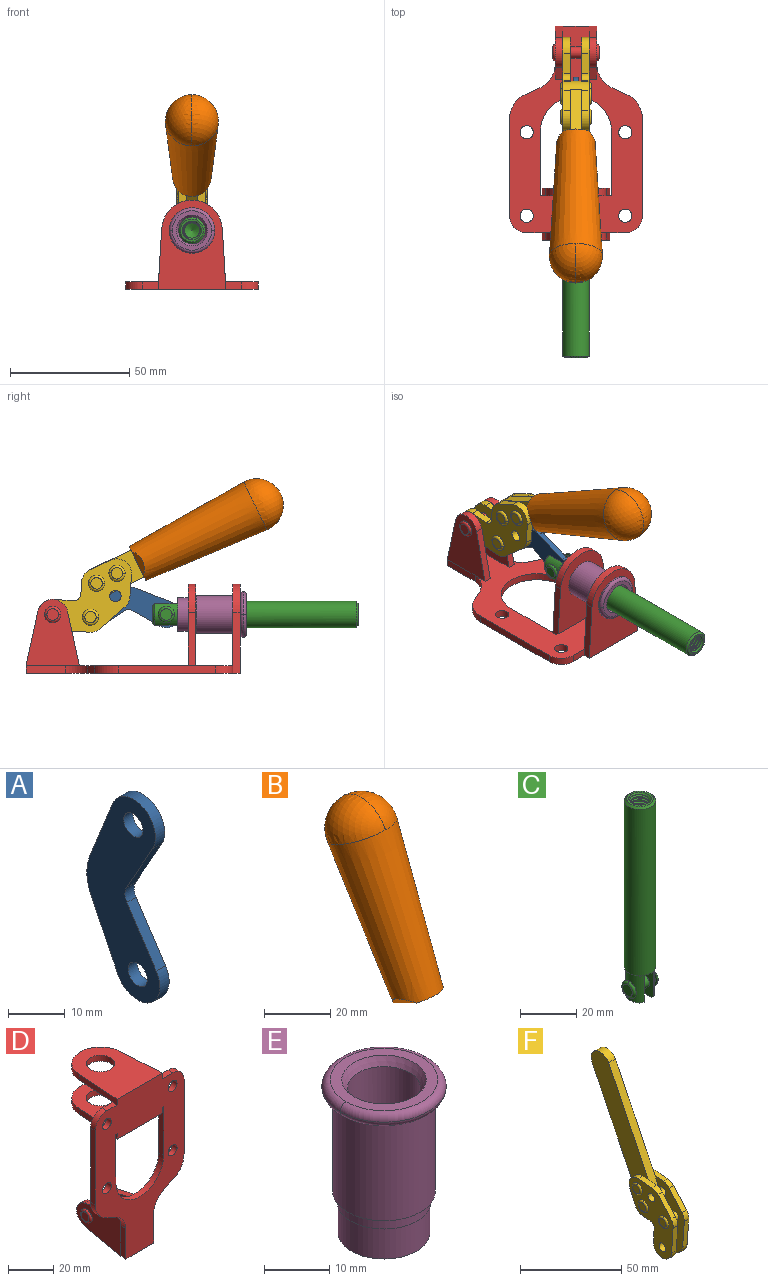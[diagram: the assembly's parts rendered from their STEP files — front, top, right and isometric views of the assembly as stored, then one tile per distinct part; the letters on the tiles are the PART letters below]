
ASSEMBLY  parts=6 mates=6
PART A: 12 faces, bbox 2.3x18.2x42.8 mm
  f0: cylinder r=2.4mm len=4.8mm, axis (1,0,0), area 34.9mm2, adj f4,f11
  f1: cylinder r=10.41mm len=8.47mm, axis (1,0,0), area 20.2mm2, adj f4,f9,f10,f11
  f2: cylinder r=3.05mm len=3.16mm, axis (1,0,0), area 7.7mm2, adj f4,f6,f7,f11
  f3: cylinder r=2.4mm len=4.8mm, axis (1,0,0), area 34.9mm2, adj f4,f11
  f4: plane 42.81x18.23mm, normal (-1,0,0), area 414.1mm2, adj f0,f1,f2,f3,f5,f6,f7,f8
  f5: cylinder r=5.54mm len=10.67mm, axis (1,0,0), area 41.8mm2, adj f4,f6,f10,f11
  f6: plane 11.66x6.53mm, normal (0,-0.87,-0.49), area 30.9mm2, adj f2,f4,f5,f11
  f7: plane 11.17x7.33mm, normal (0,-0.84,0.55), area 30.9mm2, adj f2,f4,f8,f11
  f8: cylinder r=5.54mm len=10.51mm, axis (1,0,0), area 41.8mm2, adj f4,f7,f9,f11
  f9: plane 13.67x6.67mm, normal (0,0.9,-0.44), area 35.1mm2, adj f1,f4,f8,f11
  f10: plane 14.1x5.7mm, normal (0,0.93,0.37), area 35.1mm2, adj f1,f4,f5,f11
  f11: plane 42.81x18.23mm, normal (1,0,0), area 414.1mm2, adj f0,f1,f2,f3,f5,f6,f7,f8
PART B: 11 faces, bbox 22.3x42.6x64.5 mm
  f0: sphere r=11.13mm, area 411.4mm2, adj f1,f8
  f1: cone r=11.11mm half-angle=3.3deg, axis (0,0.44,0.9), area 3251.8mm2, adj f0,f7,f8,f9,f10
  f2: cylinder r=6.16mm len=11.7mm, axis (1,0,0), area 89.5mm2, adj f3,f4,f5,f6
  f3: plane 60.23x36.75mm, normal (-1,0,0), area 763.6mm2, adj f2,f4,f6,f10
  f4: plane 51.37x25.05mm, normal (0,0.9,-0.44), area 264.2mm2, adj f2,f3,f5,f10
  f5: plane 60.23x36.75mm, normal (1,0,0), area 763.6mm2, adj f2,f4,f6,f10
  f6: plane 51.37x25.05mm, normal (0,-0.9,0.44), area 264.2mm2, adj f2,f3,f5,f10
  f7: plane 9.95x5.95mm, normal (0.71,-0.31,-0.64), area 25.8mm2, adj f1,f10
  f8: sphere r=11.13mm, area 411.4mm2, adj f0,f1
  f9: plane 9.95x5.95mm, normal (-0.71,-0.31,-0.64), area 25.8mm2, adj f1,f10
  f10: plane 14.27x11.38mm, normal (0,-0.44,-0.9), area 106.7mm2, adj f1,f3,f4,f5,f6,f7,f9
PART C: 48 faces, bbox 12.6x11.1x86.1 mm
  f0: torus R=2.41mm, axis (-1,0,0), area 15mm2, adj f30,f32,f34
  f1: torus R=2.41mm, axis (-1,0,0), area 15mm2, adj f29,f31,f33
  f2: cylinder r=5.54mm len=72.39mm, axis (0,0,1), area 2518.5mm2, adj f3,f4,f42,f43
  f3: cone r=5.54mm half-angle=45deg, axis (0,0,1), area 7.6mm2, adj f2,f5,f41
  f4: cone r=5.54mm half-angle=45deg, axis (0,0,-1), area 34.9mm2, adj f2,f39
  f5: cylinder r=5.08mm len=11.48mm, axis (0,0,1), area 108.3mm2, adj f3,f7,f8,f41
  f6: cylinder r=2.41mm len=4.83mm, axis (-1,0,0), area 71.2mm2, adj f40,f41
  f7: cylinder r=2.41mm len=4.83mm, axis (-1,0,0), area 7.6mm2, adj f5,f34
  f8: cone r=5.08mm half-angle=45deg, axis (0,0,1), area 10.6mm2, adj f5,f37,f41
  f9: cone r=3.98mm half-angle=45deg, axis (0,0,1), area 17.6mm2, adj f27,f39,f45,f46,f47
  f10: cylinder r=2.41mm len=4.83mm, axis (-1,0,0), area 7.6mm2, adj f33,f38
  f11: cylinder r=3.2mm len=6.4mm, axis (0,0,1), area 78.4mm2, adj f12,f28,f44,f45,f47
  f12: cylinder r=3.2mm len=6.4mm, axis (0,0,1), area 10.5mm2, adj f11,f13,f45,f47
  f13: cylinder r=3.2mm len=6.4mm, axis (0,0,1), area 10.5mm2, adj f12,f14,f45,f47
  f14: cylinder r=3.2mm len=6.4mm, axis (0,0,1), area 10.5mm2, adj f13,f15,f45,f47
  f15: cylinder r=3.2mm len=6.4mm, axis (0,0,1), area 10.5mm2, adj f14,f16,f45,f47
  f16: cylinder r=3.2mm len=6.4mm, axis (0,0,1), area 10.5mm2, adj f15,f17,f45,f47
  f17: cylinder r=3.2mm len=6.4mm, axis (0,0,1), area 10.5mm2, adj f16,f18,f45,f47
  f18: cylinder r=3.2mm len=6.4mm, axis (0,0,1), area 10.5mm2, adj f17,f19,f45,f47
  f19: cylinder r=3.2mm len=6.4mm, axis (0,0,1), area 10.5mm2, adj f18,f20,f45,f47
  f20: cylinder r=3.2mm len=6.4mm, axis (0,0,1), area 10.5mm2, adj f19,f21,f45,f47
  f21: cylinder r=3.2mm len=6.4mm, axis (0,0,1), area 10.5mm2, adj f20,f22,f45,f47
  f22: cylinder r=3.2mm len=6.4mm, axis (0,0,1), area 10.5mm2, adj f21,f23,f45,f47
  f23: cylinder r=3.2mm len=6.4mm, axis (0,0,1), area 10.5mm2, adj f22,f24,f45,f47
  f24: cylinder r=3.2mm len=6.4mm, axis (0,0,1), area 10.5mm2, adj f23,f25,f45,f47
  f25: cylinder r=3.2mm len=6.4mm, axis (0,0,1), area 10.5mm2, adj f24,f26,f45,f47
  f26: cylinder r=3.2mm len=6.4mm, axis (0,0,1), area 10.5mm2, adj f25,f27,f45,f47
  f27: cylinder r=3.2mm len=6.4mm, axis (0,0,1), area 7.4mm2, adj f9,f26,f45,f47
  f28: cone r=3.2mm half-angle=60deg, axis (0,0,1), area 37.2mm2, adj f11
  f29: plane 4.83x4.83mm, normal (-1,0,0), area 18.3mm2, adj f1,f31
  f30: plane 4.83x4.83mm, normal (1,0,0), area 18.3mm2, adj f0,f32
  f31: torus R=2.41mm, axis (-1,0,0), area 15mm2, adj f1,f29,f33
  f32: torus R=2.41mm, axis (-1,0,0), area 15mm2, adj f0,f30,f34
  f33: plane 6.83x6.83mm, normal (1,0,0), area 18.3mm2, adj f1,f10,f31
  f34: plane 6.83x6.83mm, normal (-1,0,0), area 18.3mm2, adj f0,f7,f32
  f35: cone r=5.08mm half-angle=45deg, axis (0,0,1), area 10.6mm2, adj f36,f38,f40
  f36: plane 7.25x1.97mm, normal (0,0,-1), area 10mm2, adj f35,f40
  f37: plane 7.25x1.97mm, normal (0,0,-1), area 10mm2, adj f8,f41
  f38: cylinder r=5.08mm len=11.48mm, axis (0,0,1), area 108.3mm2, adj f10,f35,f40,f42
  f39: plane 9.55x9.55mm, normal (0,0,1), area 22mm2, adj f4,f9
  f40: plane 12.76x10.09mm, normal (1,0,0), area 95.7mm2, adj f6,f35,f36,f38,f42,f43
  f41: plane 12.76x10.09mm, normal (-1,0,0), area 95.7mm2, adj f3,f5,f6,f8,f37,f43
  f42: cone r=5.54mm half-angle=45deg, axis (0,0,1), area 7.6mm2, adj f2,f38,f40
  f43: plane 11.07x4.7mm, normal (0,0,-1), area 50.4mm2, adj f2,f40,f41
  f44: plane 0.89x0.62mm, normal (-1,0,0), area 0.3mm2, adj f11,f45,f46,f47
  f45: bspline ~24.8x7.63mm, area 266.6mm2, adj f9,f11,f12,f13,f14,f15,f16,f17
  f46: bspline ~24.87x7.63mm, area 73.6mm2, adj f9,f44,f45,f47
  f47: bspline ~24.98x7.63mm, area 272.5mm2, adj f9,f11,f12,f13,f14,f15,f16,f17
PART D: 55 faces, bbox 55.7x37.4x89.8 mm
  f0: torus R=2.41mm, axis (-1,0,0), area 15mm2, adj f11,f15,f25
  f1: torus R=2.41mm, axis (-1,0,0), area 15mm2, adj f10,f12,f22
  f2: cylinder r=2.78mm len=5.56mm, axis (0,-1,0), area 54.2mm2, adj f30,f54
  f3: cylinder r=14.99mm len=29.97mm, axis (0,-1,0), area 145.9mm2, adj f30,f49,f53,f54
  f4: cylinder r=2.78mm len=5.56mm, axis (0,-1,0), area 54.2mm2, adj f30,f54
  f5: cylinder r=2.78mm len=5.56mm, axis (0,-1,0), area 54.2mm2, adj f30,f54
  f6: cylinder r=2.78mm len=5.56mm, axis (0,-1,0), area 54.2mm2, adj f30,f54
  f7: cylinder r=6.35mm len=12.7mm, axis (0,0,1), area 123.6mm2, adj f27,f51
  f8: cylinder r=6.35mm len=12.7mm, axis (0,0,-1), area 124.7mm2, adj f21,f35
  f9: cylinder r=2.41mm len=11.18mm, axis (-1,0,0), area 169.4mm2, adj f16,f19
  f10: plane 4.83x4.83mm, normal (1,0,0), area 18.3mm2, adj f1,f12
  f11: plane 4.83x4.83mm, normal (-1,0,0), area 18.3mm2, adj f0,f15
  f12: torus R=2.41mm, axis (-1,0,0), area 15mm2, adj f1,f10,f22
  f13: cylinder r=6.35mm len=12.41mm, axis (1,0,0), area 53.4mm2, adj f18,f19,f22,f23
  f14: cylinder r=6.35mm len=12.41mm, axis (-1,0,0), area 53.4mm2, adj f16,f17,f24,f25
  f15: torus R=2.41mm, axis (-1,0,0), area 15mm2, adj f0,f11,f25
  f16: plane 27.86x22.35mm, normal (1,0,0), area 425.4mm2, adj f9,f14,f17,f24,f30
  f17: plane 22.86x4.97mm, normal (0,0.21,0.98), area 72.5mm2, adj f14,f16,f25,f30
  f18: plane 22.86x4.97mm, normal (0,0.21,0.98), area 72.5mm2, adj f13,f19,f22,f30
  f19: plane 27.86x22.35mm, normal (-1,0,0), area 425.4mm2, adj f9,f13,f18,f23,f30
  f20: cylinder r=12.7mm len=25.35mm, axis (0,0,-1), area 119.8mm2, adj f21,f34,f35,f36
  f21: plane 34.21x28.07mm, normal (0,0,-1), area 702.4mm2, adj f8,f20,f30,f34,f36
  f22: plane 27.96x22.45mm, normal (1,0,0), area 407.2mm2, adj f1,f12,f13,f18,f23,f30,f42,f43
  f23: plane 22.86x4.97mm, normal (0,0.21,-0.98), area 72.5mm2, adj f13,f19,f22,f44
  f24: plane 22.86x4.97mm, normal (0,0.21,-0.98), area 72.5mm2, adj f14,f16,f25,f44
  f25: plane 27.86x22.35mm, normal (-1,0,0), area 407.1mm2, adj f0,f14,f15,f17,f24,f30,f45,f46
  f26: plane 3.1x0.95mm, normal (0,0,-1), area 2.7mm2, adj f30,f49,f50,f54
  f27: plane 34.21x28.07mm, normal (0,0,1), area 702.4mm2, adj f7,f28,f30,f50,f52
  f28: cylinder r=12.7mm len=25.35mm, axis (0,0,1), area 118.8mm2, adj f27,f50,f51,f52
  f29: plane 3.1x0.95mm, normal (0,0,-1), area 2.7mm2, adj f30,f52,f53,f54
  f30: plane 86.54x55.63mm, normal (0,1,0), area 2362.9mm2, adj f2,f3,f4,f5,f6,f16,f17,f18
  f31: plane 40.56x3.1mm, normal (-1,0,0), area 125.7mm2, adj f30,f32,f48,f54
  f32: cylinder r=7.11mm len=7.11mm, axis (0,-1,0), area 34.6mm2, adj f30,f31,f33,f54
  f33: plane 6.67x3.1mm, normal (0,0,1), area 20.4mm2, adj f30,f32,f34,f54
  f34: plane 25.39x3.13mm, normal (-1,0.06,0), area 79.5mm2, adj f20,f21,f33,f35,f54
  f35: plane 37.31x28.45mm, normal (0,0,1), area 789.9mm2, adj f8,f20,f34,f36,f54
  f36: plane 25.39x3.13mm, normal (1,0.06,0), area 79.5mm2, adj f20,f21,f35,f37,f54
  f37: plane 6.67x3.1mm, normal (0,0,1), area 20.4mm2, adj f30,f36,f38,f54
  f38: cylinder r=7.11mm len=7.11mm, axis (0,-1,0), area 34.6mm2, adj f30,f37,f39,f54
  f39: plane 40.56x3.1mm, normal (1,0,0), area 125.7mm2, adj f30,f38,f40,f54
  f40: cylinder r=11.18mm len=10.16mm, axis (0,-1,0), area 39.5mm2, adj f30,f39,f41,f54
  f41: plane 6.09x3.1mm, normal (0.42,0,-0.91), area 20.8mm2, adj f30,f40,f42,f54
  f42: cylinder r=11.18mm len=9.41mm, axis (0,-1,0), area 37.2mm2, adj f22,f30,f41,f43,f54
  f43: plane 16.5x3.1mm, normal (1,0,0), area 51.1mm2, adj f22,f42,f44,f54
  f44: plane 17.37x3.1mm, normal (0,0,-1), area 53.8mm2, adj f23,f24,f30,f43,f45,f54
  f45: plane 16.5x3.1mm, normal (-1,0,0), area 51.1mm2, adj f25,f44,f46,f54
  f46: cylinder r=11.18mm len=9.41mm, axis (0,-1,0), area 37.2mm2, adj f25,f30,f45,f47,f54
  f47: plane 6.09x3.1mm, normal (-0.42,0,-0.91), area 20.8mm2, adj f30,f46,f48,f54
  f48: cylinder r=11.18mm len=10.16mm, axis (0,-1,0), area 39.5mm2, adj f30,f31,f47,f54
  f49: plane 26.54x3.1mm, normal (-1,0,0), area 82.3mm2, adj f3,f26,f30,f54
  f50: plane 25.39x3.1mm, normal (1,0.06,0), area 78.8mm2, adj f26,f27,f28,f51,f54
  f51: plane 37.31x28.45mm, normal (0,0,-1), area 789.9mm2, adj f7,f28,f50,f52,f54
  f52: plane 25.39x3.1mm, normal (-1,0.06,0), area 78.8mm2, adj f27,f28,f29,f51,f54
  f53: plane 26.54x3.1mm, normal (1,0,0), area 82.3mm2, adj f3,f29,f30,f54
  f54: plane 89.66x55.63mm, normal (0,-1,0), area 2678.5mm2, adj f2,f3,f4,f5,f6,f26,f29,f31
PART E: 15 faces, bbox 20.6x20.6x28.7 mm
  f0: torus R=8.26mm, axis (0,0,1), area 56.8mm2, adj f1,f10,f12
  f1: torus R=8.26mm, axis (0,0,1), area 56.8mm2, adj f0,f6,f13
  f2: cylinder r=5.59mm len=25.91mm, axis (0,0,1), area 909.6mm2, adj f3,f4
  f3: cone r=6.86mm half-angle=45deg, axis (0,0,-1), area 70.2mm2, adj f2,f14
  f4: cone r=6.47mm half-angle=30deg, axis (0,0,1), area 66.7mm2, adj f2,f13
  f5: cylinder r=7.04mm len=14.07mm, axis (0,0,1), area 252.6mm2, adj f11,f14
  f6: torus R=8.26mm, axis (0,0,1), area 56.8mm2, adj f1,f12,f13
  f7: cylinder r=7.16mm len=14.33mm, axis (0,0,1), area 91.5mm2, adj f9,f11
  f8: cylinder r=7.86mm len=18.42mm, axis (0,0,1), area 909.6mm2, adj f9,f10
  f9: plane 15.72x15.72mm, normal (0,0,-1), area 33mm2, adj f7,f8
  f10: plane 16.51x16.51mm, normal (0,0,-1), area 19.9mm2, adj f0,f8,f12
  f11: plane 14.33x14.33mm, normal (0,0,-1), area 5.7mm2, adj f5,f7
  f12: torus R=8.26mm, axis (0,0,1), area 56.8mm2, adj f0,f6,f10
  f13: plane 16.51x16.51mm, normal (0,0,1), area 82.7mm2, adj f1,f4,f6
  f14: plane 14.07x14.07mm, normal (0,0,-1), area 7.8mm2, adj f3,f5
PART F: 59 faces, bbox 12.9x60.2x99.6 mm
  f0: torus R=2.39mm, axis (-1,0,0), area 14.9mm2, adj f20,f43,f51
  f1: torus R=2.39mm, axis (-1,0,0), area 14.9mm2, adj f19,f42,f51
  f2: torus R=2.39mm, axis (-1,0,0), area 14.9mm2, adj f18,f35,f51
  f3: torus R=2.39mm, axis (-1,0,0), area 14.9mm2, adj f14,f17,f23
  f4: torus R=2.39mm, axis (-1,0,0), area 14.9mm2, adj f13,f16,f23
  f5: torus R=2.39mm, axis (-1,0,0), area 14.9mm2, adj f12,f15,f23
  f6: cylinder r=2.39mm len=4.78mm, axis (1,0,0), area 46.5mm2, adj f48,f50,f51
  f7: cylinder r=2.39mm len=4.78mm, axis (1,0,0), area 46.5mm2, adj f50,f51
  f8: cylinder r=6.35mm len=12.68mm, axis (1,0,0), area 61.8mm2, adj f38,f39,f50,f51
  f9: cylinder r=2.39mm len=4.78mm, axis (-1,0,0), area 70.5mm2, adj f46,f50
  f10: cylinder r=2.39mm len=4.78mm, axis (-1,0,0), area 46.5mm2, adj f23,f45,f46
  f11: cylinder r=2.39mm len=4.78mm, axis (-1,0,0), area 46.5mm2, adj f23,f46
  f12: plane 4.78x4.78mm, normal (1,0,0), area 17.9mm2, adj f5,f15
  f13: plane 4.78x4.78mm, normal (1,0,0), area 17.9mm2, adj f4,f16
  f14: plane 4.78x4.78mm, normal (1,0,0), area 17.9mm2, adj f3,f17
  f15: torus R=2.39mm, axis (-1,0,0), area 14.9mm2, adj f5,f12,f23
  f16: torus R=2.39mm, axis (-1,0,0), area 14.9mm2, adj f4,f13,f23
  f17: torus R=2.39mm, axis (-1,0,0), area 14.9mm2, adj f3,f14,f23
  f18: plane 4.78x4.78mm, normal (-1,0,0), area 17.9mm2, adj f2,f35
  f19: plane 4.78x4.78mm, normal (-1,0,0), area 17.9mm2, adj f1,f42
  f20: plane 4.78x4.78mm, normal (-1,0,0), area 17.9mm2, adj f0,f43
  f21: plane 2.26x0.2mm, normal (1,0,0), area 0.2mm2, adj f31,f44
  f22: plane 2.26x0.2mm, normal (-1,0,0), area 0.2mm2, adj f41,f44
  f23: plane 39.37x30.77mm, normal (1,0,0), area 565.5mm2, adj f3,f4,f5,f10,f11,f15,f16,f17
  f24: cylinder r=6.1mm len=4.15mm, axis (-1,0,0), area 14.7mm2, adj f23,f25,f32,f46
  f25: plane 10.25x9.01mm, normal (0,-0.75,0.66), area 42.3mm2, adj f23,f24,f26,f46
  f26: cylinder r=6.35mm len=4.64mm, axis (-1,0,0), area 15.6mm2, adj f23,f25,f27,f46
  f27: plane 15.84x3.1mm, normal (0,-1,-0.07), area 49.2mm2, adj f23,f26,f28,f46
  f28: cylinder r=6.35mm len=12.68mm, axis (-1,0,0), area 61.8mm2, adj f23,f27,f29,f46
  f29: plane 8.11x3.1mm, normal (0,1,0.07), area 25.2mm2, adj f23,f28,f30,f46
  f30: cylinder r=3.05mm len=3.25mm, axis (-1,0,0), area 14.8mm2, adj f23,f29,f31,f46
  f31: plane 5.99x3.1mm, normal (0,0.07,-1), area 18.6mm2, adj f21,f23,f30,f44,f46
  f32: plane 9.5x3.1mm, normal (0,-0.07,1), area 29.5mm2, adj f23,f24,f33,f46,f47
  f33: cylinder r=6.1mm len=8.63mm, axis (-1,0,0), area 39.1mm2, adj f23,f32,f34,f47
  f34: plane 8.65x3.96mm, normal (0,0.91,-0.42), area 29.5mm2, adj f23,f33,f44,f47
  f35: torus R=2.39mm, axis (-1,0,0), area 14.9mm2, adj f2,f18,f51
  f36: plane 10.25x9.01mm, normal (0,-0.75,0.66), area 42.3mm2, adj f37,f49,f50,f51
  f37: cylinder r=6.35mm len=4.64mm, axis (1,0,0), area 15.6mm2, adj f36,f38,f50,f51
  f38: plane 15.84x3.1mm, normal (0,-1,-0.07), area 49.2mm2, adj f8,f37,f50,f51
  f39: plane 8.11x3.1mm, normal (0,1,0.07), area 25.2mm2, adj f8,f40,f50,f51
  f40: cylinder r=3.05mm len=3.25mm, axis (1,0,0), area 14.8mm2, adj f39,f41,f50,f51
  f41: plane 5.99x3.1mm, normal (0,0.07,-1), area 18.6mm2, adj f22,f40,f44,f50,f51
  f42: torus R=2.39mm, axis (-1,0,0), area 14.9mm2, adj f1,f19,f51
  f43: torus R=2.39mm, axis (-1,0,0), area 14.9mm2, adj f0,f20,f51
  f44: cylinder r=6.35mm len=12.12mm, axis (-1,0,0), area 128.9mm2, adj f21,f22,f23,f31,f34,f41,f46,f47
  f45: plane 2.65x1.35mm, normal (1,0,0), area 1mm2, adj f10,f55
  f46: plane 39.08x20.42mm, normal (-1,0,0), area 412.5mm2, adj f9,f10,f11,f24,f25,f26,f27,f28
  f47: plane 77.62x39.82mm, normal (1,0,0), area 850mm2, adj f32,f33,f34,f44,f53,f54,f55
  f48: plane 2.65x1.35mm, normal (-1,0,0), area 1mm2, adj f6,f55
  f49: cylinder r=6.1mm len=4.15mm, axis (1,0,0), area 14.7mm2, adj f36,f50,f51,f56
  f50: plane 39.08x20.42mm, normal (1,0,0), area 412.5mm2, adj f6,f7,f8,f9,f36,f37,f38,f39
  f51: plane 39.37x30.77mm, normal (-1,0,0), area 565.5mm2, adj f0,f1,f2,f6,f7,f8,f35,f36
  f52: plane 8.65x3.96mm, normal (0,0.91,-0.42), area 29.5mm2, adj f44,f51,f57,f58
  f53: plane 68.49x33.4mm, normal (0,0.9,-0.44), area 358.1mm2, adj f44,f47,f54,f58
  f54: cylinder r=6.35mm len=12.06mm, axis (1,0,0), area 93.7mm2, adj f47,f53,f55,f58
  f55: plane 68.49x33.4mm, normal (0,-0.9,0.44), area 358.1mm2, adj f44,f45,f46,f47,f48,f50,f54,f58
  f56: plane 9.5x3.1mm, normal (0,-0.07,1), area 29.5mm2, adj f49,f50,f51,f57,f58
  f57: cylinder r=6.1mm len=8.63mm, axis (1,0,0), area 39.1mm2, adj f51,f52,f56,f58
  f58: plane 77.62x39.82mm, normal (-1,0,0), area 850mm2, adj f44,f52,f53,f54,f55,f56,f57
PLACE A rot(axis=(1,0,0),90deg) t=(0,9.14,0)mm
PLACE B rot(axis=(1,0,0),90deg) t=(-0.04,9.14,0)mm
PLACE C rot(axis=(1,0,0),90deg) t=(0,9.14,0)mm
PLACE D rot(axis=(1,0,0),90deg) t=(0,9.14,0)mm fixed
PLACE E rot(axis=(1,0,0),90deg) t=(0,9.14,0)mm
PLACE F rot(axis=(1,0,0),90deg) t=(0,9.14,0)mm
MATE revolute A.f3 <-> F.f4  axis (1,0,0) through (0,25.4,23.5)mm
MATE fastened E.f0 <-> D.f7  axis (0,1,0) through (0,-37.25,24.61)mm
MATE slider C.f2 <-> E.f2  axis (0,-1,0) through (0,-49.64,24.61)mm
MATE fastened B.f2 <-> F.f54  axis (1,0,0) through (-2.35,-45.63,71.04)mm
MATE revolute F.f7 <-> D.f0  axis (-1,0,0) through (0,41.23,24.61)mm
MATE fastened A.f5 <-> C.f6  axis (1,0,0) through (0,-6.33,24.61)mm
